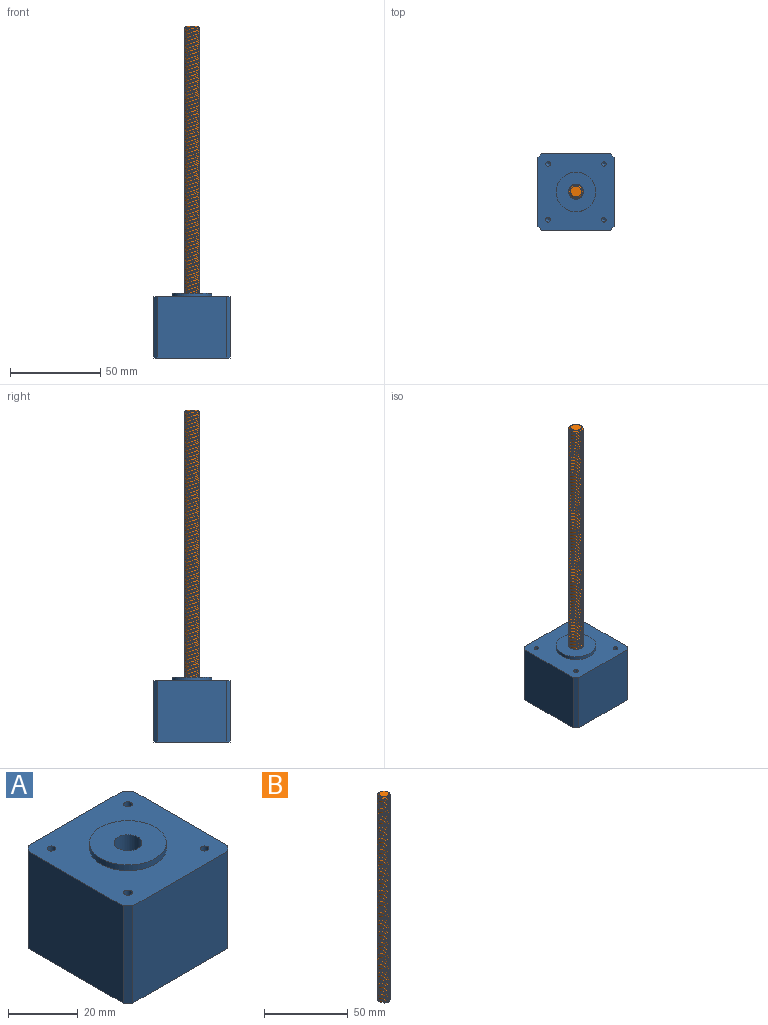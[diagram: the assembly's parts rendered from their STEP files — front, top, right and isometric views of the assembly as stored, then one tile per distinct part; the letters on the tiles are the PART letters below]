
ASSEMBLY  parts=2 mates=1
PART A: 21 faces, bbox 42.3x42.3x36 mm
  f0: plane 38.3x34mm, normal (0,1,0), area 1302.2mm2, adj f5,f6,f17,f19
  f1: plane 38.3x34mm, normal (-1,0,0), area 1302.2mm2, adj f5,f6,f17,f18
  f2: plane 38.3x34mm, normal (0,-1,0), area 1302.2mm2, adj f5,f6,f18,f20
  f3: plane 38.3x34mm, normal (1,0,0), area 1302.2mm2, adj f5,f6,f19,f20
  f4: cylinder r=4mm len=36mm, axis (0,0,1), area 904.8mm2, adj f5,f8
  f5: plane 42.3x42.3mm, normal (0,0,-1), area 1731mm2, adj f0,f1,f2,f3,f4,f17,f18,f19
  f6: plane 42.3x42.3mm, normal (0,0,1), area 1381.5mm2, adj f0,f1,f2,f3,f7,f10,f12,f14
  f7: cylinder r=11mm len=22mm, axis (0,0,-1), area 138.2mm2, adj f6,f8
  f8: plane 22x22mm, normal (0,0,1), area 329.9mm2, adj f4,f7
  f9: cone r=0mm half-angle=59deg, axis (0,0,1), area 5.7mm2, adj f10
  f10: cylinder r=1.25mm len=5.5mm, axis (0,0,1), area 43.2mm2, adj f6,f9
  f11: cone r=0mm half-angle=59deg, axis (0,0,1), area 5.7mm2, adj f12
  f12: cylinder r=1.25mm len=5.5mm, axis (0,0,1), area 43.2mm2, adj f6,f11
  f13: cone r=0mm half-angle=59deg, axis (0,0,1), area 5.7mm2, adj f14
  f14: cylinder r=1.25mm len=5.5mm, axis (0,0,1), area 43.2mm2, adj f6,f13
  f15: cone r=0mm half-angle=59deg, axis (0,0,1), area 5.7mm2, adj f16
  f16: cylinder r=1.25mm len=5.5mm, axis (0,0,1), area 43.2mm2, adj f6,f15
  f17: plane 34x2mm, normal (-0.71,0.71,0), area 96.2mm2, adj f0,f1,f5,f6
  f18: plane 34x2mm, normal (-0.71,-0.71,0), area 96.2mm2, adj f1,f2,f5,f6
  f19: plane 34x2mm, normal (0.71,0.71,0), area 96.2mm2, adj f0,f3,f5,f6
  f20: plane 34x2mm, normal (0.71,-0.71,0), area 96.2mm2, adj f2,f3,f5,f6
PART B: 22 faces, bbox 8x8x152 mm
  f0: cylinder r=4mm len=149mm, axis (0,0,-1), area 467.6mm2, adj f1,f9,f10,f20
  f1: plane 8.03x8.03mm, normal (0,0,-1), area 42.2mm2, adj f0,f3,f5,f7,f10,f11,f12,f13
  f2: cone r=3mm half-angle=45deg, axis (0,0,-1), area 4.9mm2, adj f3,f8,f17,f19
  f3: cylinder r=4mm len=149mm, axis (0,0,-1), area 467.6mm2, adj f1,f2,f17,f19
  f4: cone r=3mm half-angle=45deg, axis (0,0,-1), area 4.9mm2, adj f5,f8,f14,f16
  f5: cylinder r=4mm len=149mm, axis (0,0,-1), area 467.6mm2, adj f1,f4,f14,f16
  f6: cone r=3mm half-angle=45deg, axis (0,0,-1), area 4.9mm2, adj f7,f8,f11,f13
  f7: cylinder r=4mm len=149mm, axis (0,0,-1), area 467.6mm2, adj f1,f6,f11,f13
  f8: plane 6x6mm, normal (0,0,1), area 28.3mm2, adj f2,f4,f6,f9,f12,f15,f18,f21
  f9: cone r=3mm half-angle=45deg, axis (0,0,-1), area 4.9mm2, adj f0,f8,f10,f20
  f10: bspline ~151.27x8mm, area 450.8mm2, adj f0,f1,f9,f12
  f11: bspline ~151.27x8mm, area 450.8mm2, adj f1,f6,f7,f12
  f12: cylinder r=3mm len=150mm, axis (0,0,1), area 231.5mm2, adj f1,f8,f10,f11
  f13: bspline ~151.27x8mm, area 450.8mm2, adj f1,f6,f7,f15
  f14: bspline ~151.27x8mm, area 450.8mm2, adj f1,f4,f5,f15
  f15: cylinder r=3mm len=150mm, axis (0,0,1), area 231.5mm2, adj f1,f8,f13,f14
  f16: bspline ~151.27x8mm, area 450.8mm2, adj f1,f4,f5,f18
  f17: bspline ~151.27x8mm, area 450.8mm2, adj f1,f2,f3,f18
  f18: cylinder r=3mm len=150mm, axis (0,0,1), area 231.5mm2, adj f1,f8,f16,f17
  f19: bspline ~151.27x8mm, area 450.8mm2, adj f1,f2,f3,f21
  f20: bspline ~151.27x8mm, area 450.8mm2, adj f0,f1,f9,f21
  f21: cylinder r=3mm len=150mm, axis (0,0,1), area 231.5mm2, adj f1,f8,f19,f20
PLACE A at identity fixed
PLACE B rot(axis=(0,0,-1),90deg) t=(0,0,0)mm
MATE revolute B.f0 <-> A.f7  axis (0,0,-1) through (0,0,0)mm
